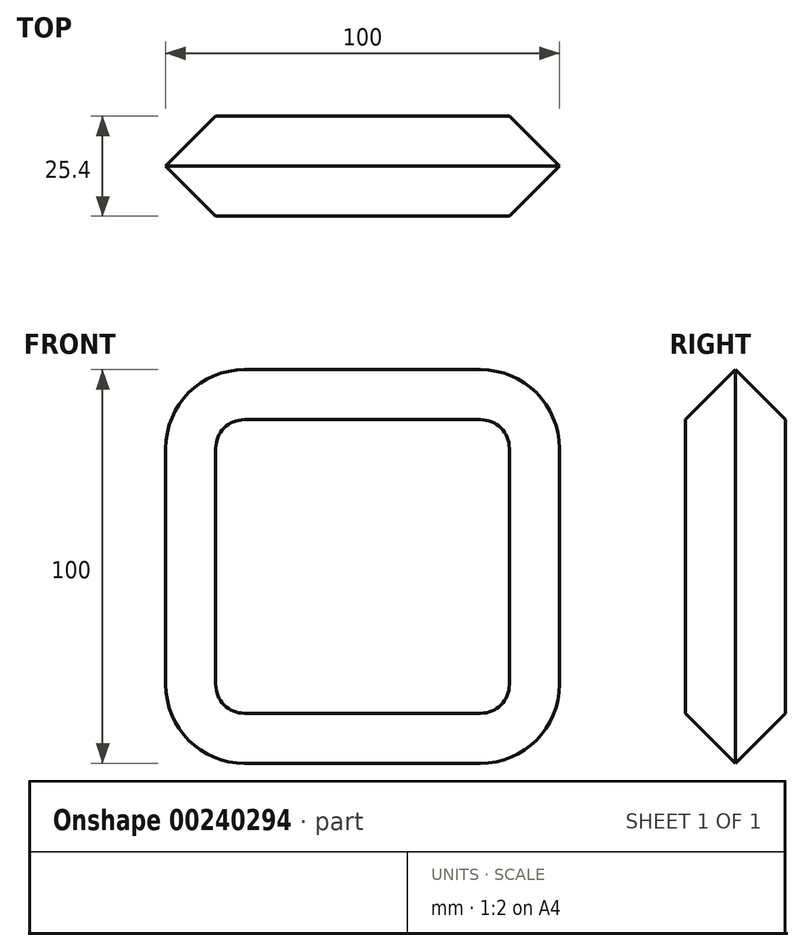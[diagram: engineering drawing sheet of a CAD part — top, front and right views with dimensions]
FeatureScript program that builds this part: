
annotation { "Feature Type Name" : "Feature", "Feature Type Description" : "" }
export const myFeature = defineFeature(function(context is Context, id is Id, definition is map)
    precondition{}
    {
        {
            var Q0;
            Q0=qCreatedBy(makeId("Front.planeOp"),FACE);
            var sketch = newSketch(context, id + "F0", { "sketchPlane" : qUnion([Q0])});
            skLineSegment(sketch, "E0.bottom", {"start": v(30, -50) * mm, "end": v(-30, -50) * mm});
            skLineSegment(sketch, "E0.top", {"start": v(30, 50) * mm, "end": v(-30, 50) * mm});
            skLineSegment(sketch, "E0.left", {"start": v(50, -30) * mm, "end": v(50, 30) * mm});
            skLineSegment(sketch, "E0.right", {"start": v(-50, -30) * mm, "end": v(-50, 30) * mm});
            skPoint(sketch, "E0.middle", {"position": v(0, 0) * mm});
            skPoint(sketch, "E1.visualSharp", {"position": v(-50, 50) * mm});
            skArc(sketch, "E1.filletArc", {"start": v(-30, 50) * mm, "mid": v(-44.14, 44.14) * mm, "end": v(-50, 30) * mm});
            skPoint(sketch, "E2.visualSharp", {"position": v(50, 50) * mm});
            skArc(sketch, "E2.filletArc", {"start": v(50, 30) * mm, "mid": v(44.14, 44.14) * mm, "end": v(30, 50) * mm});
            skPoint(sketch, "E3.visualSharp", {"position": v(50, -50) * mm});
            skArc(sketch, "E3.filletArc", {"start": v(30, -50) * mm, "mid": v(44.14, -44.14) * mm, "end": v(50, -30) * mm});
            skPoint(sketch, "E4.visualSharp", {"position": v(-50, -50) * mm});
            skArc(sketch, "E4.filletArc", {"start": v(-50, -30) * mm, "mid": v(-44.14, -44.14) * mm, "end": v(-30, -50) * mm});
            skSolve(sketch);
        }
        {
            var Q0;
            Q0=makeQuery(id+"F0.imprint","IMPRINT",FACE,{"disambiguationData":[TD([[makeQuery(id+"F0.imprint","IMPRINT",EDGE,{"derivedFrom":sQuery(id+"F0.wireOp",EDGE,"E0.bottom")}),-1.0]])]});
            extrude(context, id + "F1", {"entities" : qUnion([Q0]), "depth" : 25.4 * mm});
        }
        {
            var Q0;
            Q0=makeQuery(id+"F1.opExtrude","CAP_FACE",FACE,{"disambiguationData":[OSD([sQuery(id+"F0.wireOp",EDGE,"E0.bottom"),sQuery(id+"F0.wireOp",EDGE,"E0.top"),sQuery(id+"F0.wireOp",EDGE,"E0.left"),sQuery(id+"F0.wireOp",EDGE,"E0.right"),sQuery(id+"F0.wireOp",EDGE,"E1.filletArc"),sQuery(id+"F0.wireOp",EDGE,"E2.filletArc"),sQuery(id+"F0.wireOp",EDGE,"E3.filletArc"),sQuery(id+"F0.wireOp",EDGE,"E4.filletArc")])],"isStart":false});
            var Q1;
            Q1=makeQuery(id+"F1.opExtrude","CAP_FACE",FACE,{"disambiguationData":[OSD([sQuery(id+"F0.wireOp",EDGE,"E0.bottom"),sQuery(id+"F0.wireOp",EDGE,"E0.top"),sQuery(id+"F0.wireOp",EDGE,"E0.left"),sQuery(id+"F0.wireOp",EDGE,"E0.right"),sQuery(id+"F0.wireOp",EDGE,"E1.filletArc"),sQuery(id+"F0.wireOp",EDGE,"E2.filletArc"),sQuery(id+"F0.wireOp",EDGE,"E3.filletArc"),sQuery(id+"F0.wireOp",EDGE,"E4.filletArc")])],"isStart":true});
            chamfer(context, id + "F2", {"entities" : qUnion([Q0, Q1]), "width" : 12.7 * mm, "tangentPropagation" : true});
        }
    });
